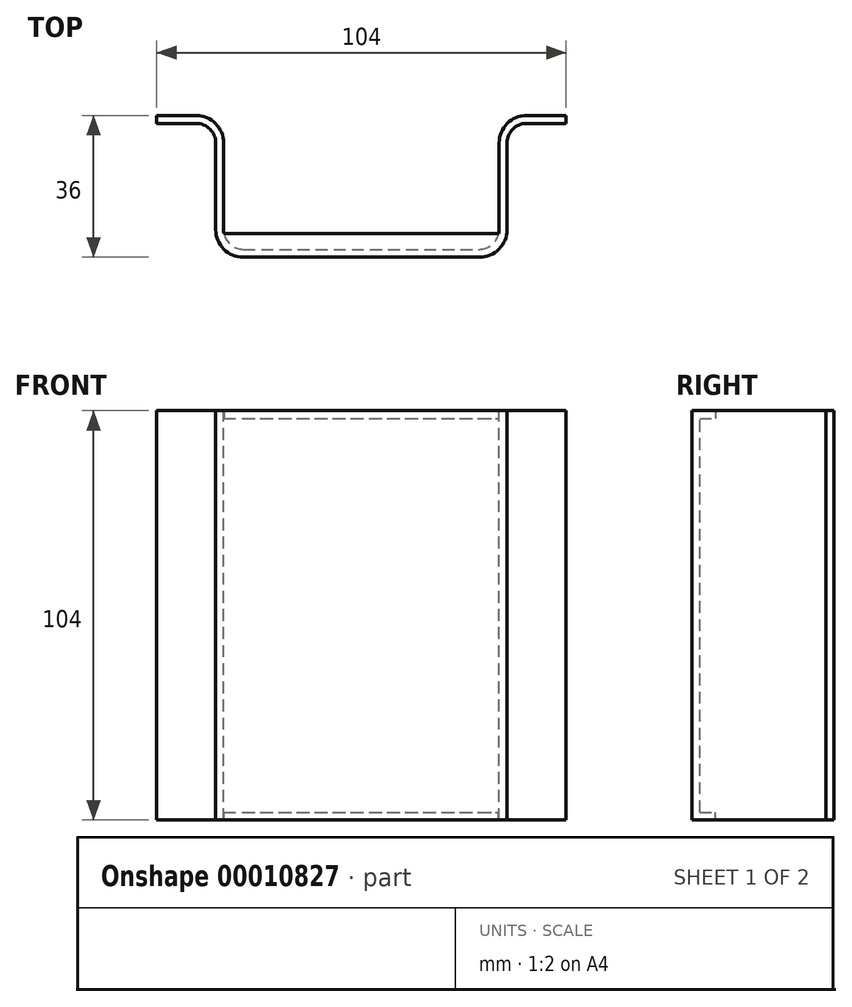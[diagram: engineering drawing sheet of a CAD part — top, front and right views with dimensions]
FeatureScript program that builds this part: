
annotation { "Feature Type Name" : "Feature", "Feature Type Description" : "" }
export const myFeature = defineFeature(function(context is Context, id is Id, definition is map)
    precondition{}
    {
        {
            var Q0;
            Q0=qCreatedBy(makeId("Top.planeOp"),FACE);
            var sketch = newSketch(context, id + "F0", { "sketchPlane" : qUnion([Q0])});
            skLineSegment(sketch, "E0", {"start": v(0, 0) * mm, "end": v(30, 0) * mm});
            skLineSegment(sketch, "E1", {"start": v(37, 7) * mm, "end": v(37, 29) * mm});
            skLineSegment(sketch, "E2", {"start": v(42, 34) * mm, "end": v(52, 34) * mm});
            skLineSegment(sketch, "E3.0", {"start": v(42, 36) * mm, "end": v(52, 36) * mm});
            skLineSegment(sketch, "E3.1", {"start": v(35, 7) * mm, "end": v(35, 29) * mm});
            skLineSegment(sketch, "E3.2", {"start": v(0, 2) * mm, "end": v(30, 2) * mm});
            skLineSegment(sketch, "E4", {"start": v(0, 2) * mm, "end": v(0, 0) * mm, "construction": true});
            skLineSegment(sketch, "E5", {"start": v(52, 36) * mm, "end": v(52, 34) * mm});
            skPoint(sketch, "E6.visualSharp", {"position": v(35, 2) * mm});
            skArc(sketch, "E6.filletArc", {"start": v(30, 2) * mm, "mid": v(33.54, 3.46) * mm, "end": v(35, 7) * mm});
            skPoint(sketch, "E7.visualSharp", {"position": v(37, 0) * mm});
            skArc(sketch, "E7.filletArc", {"start": v(30, 0) * mm, "mid": v(34.95, 2.05) * mm, "end": v(37, 7) * mm});
            skPoint(sketch, "E8.visualSharp", {"position": v(37, 34) * mm});
            skArc(sketch, "E8.filletArc", {"start": v(42, 34) * mm, "mid": v(38.46, 32.54) * mm, "end": v(37, 29) * mm});
            skPoint(sketch, "E9.visualSharp", {"position": v(35, 36) * mm});
            skArc(sketch, "E9.filletArc", {"start": v(42, 36) * mm, "mid": v(37.05, 33.95) * mm, "end": v(35, 29) * mm});
            skLineSegment(sketch, "E10.0.MirrorCS", {"start": v(0, 2) * mm, "end": v(-30, 2) * mm});
            skLineSegment(sketch, "E11.0.MirrorCS", {"start": v(0, 0) * mm, "end": v(-30, 0) * mm});
            skArc(sketch, "E12.0.MirrorCS", {"start": v(-30, 2) * mm, "mid": v(-33.54, 3.46) * mm, "end": v(-35, 7) * mm});
            skArc(sketch, "E13.0.MirrorCS", {"start": v(-30, 0) * mm, "mid": v(-34.95, 2.05) * mm, "end": v(-37, 7) * mm});
            skLineSegment(sketch, "E14.0.MirrorCS", {"start": v(-35, 7) * mm, "end": v(-35, 29) * mm});
            skLineSegment(sketch, "E15.0.MirrorCS", {"start": v(-37, 7) * mm, "end": v(-37, 29) * mm});
            skArc(sketch, "E16.0.MirrorCS", {"start": v(-42, 36) * mm, "mid": v(-37.05, 33.95) * mm, "end": v(-35, 29) * mm});
            skArc(sketch, "E17.0.MirrorCS", {"start": v(-42, 34) * mm, "mid": v(-38.46, 32.54) * mm, "end": v(-37, 29) * mm});
            skLineSegment(sketch, "E18.0.MirrorCS", {"start": v(-42, 36) * mm, "end": v(-52, 36) * mm});
            skLineSegment(sketch, "E19.0.MirrorCS", {"start": v(-42, 34) * mm, "end": v(-52, 34) * mm});
            skLineSegment(sketch, "E20.0.MirrorCS", {"start": v(-52, 36) * mm, "end": v(-52, 34) * mm});
            skLineSegment(sketch, "E21", {"start": v(-34.9, 6) * mm, "end": v(34.9, 6) * mm});
            skSolve(sketch);
        }
        {
            var Q0;
            Q0=makeQuery(id+"F0.imprint","IMPRINT",FACE,{"disambiguationData":[TD([[makeQuery(id+"F0.imprint","IMPRINT",EDGE,{"derivedFrom":sQuery(id+"F0.wireOp",EDGE,"E0")}),1.0]])]});
            extrude(context, id + "F1", {"entities" : qUnion([Q0]), "oppositeDirection" : true, "depth" : (100 / 2) * mm});
        }
        {
            var Q0;
            Q0=makeQuery(id+"F0.imprint","IMPRINT",FACE,{"disambiguationData":[TD([[makeQuery(id+"F0.imprint","IMPRINT",EDGE,{"derivedFrom":sQuery(id+"F0.wireOp",EDGE,"E0")}),1.0]])]});
            var Q1;
            {var subQ4=sQuery(id+"F0.wireOp",EDGE,"E3.2");Q1=makeQuery(id+"F0.imprint","IMPRINT",FACE,{"disambiguationData":[TD([[makeQuery(id+"F0.imprint","IMPRINT",EDGE,{"derivedFrom":subQ4}),1.0]])]});}
            extrude(context, id + "F2", {"entities" : qUnion([Q0, Q1]), "operationType" : NewBodyOperationType.ADD, "depth" : 2 * mm});
        }
        {
            var Q0;
            Q0=makeQuery(id+"F1.opExtrude","SWEPT_BODY",BODY,{"disambiguationData":[OSD([sQuery(id+"F0.wireOp",EDGE,"E0"),sQuery(id+"F0.wireOp",EDGE,"E1"),sQuery(id+"F0.wireOp",EDGE,"E2"),sQuery(id+"F0.wireOp",EDGE,"E3.0"),sQuery(id+"F0.wireOp",EDGE,"E3.1"),sQuery(id+"F0.wireOp",EDGE,"E3.2"),sQuery(id+"F0.wireOp",EDGE,"E5"),sQuery(id+"F0.wireOp",EDGE,"E6.filletArc"),sQuery(id+"F0.wireOp",EDGE,"E7.filletArc"),sQuery(id+"F0.wireOp",EDGE,"E8.filletArc"),sQuery(id+"F0.wireOp",EDGE,"E9.filletArc"),sQuery(id+"F0.wireOp",EDGE,"E10.0.MirrorCS"),sQuery(id+"F0.wireOp",EDGE,"E11.0.MirrorCS"),sQuery(id+"F0.wireOp",EDGE,"E12.0.MirrorCS"),sQuery(id+"F0.wireOp",EDGE,"E13.0.MirrorCS"),sQuery(id+"F0.wireOp",EDGE,"E14.0.MirrorCS"),sQuery(id+"F0.wireOp",EDGE,"E15.0.MirrorCS"),sQuery(id+"F0.wireOp",EDGE,"E16.0.MirrorCS"),sQuery(id+"F0.wireOp",EDGE,"E17.0.MirrorCS"),sQuery(id+"F0.wireOp",EDGE,"E18.0.MirrorCS"),sQuery(id+"F0.wireOp",EDGE,"E19.0.MirrorCS"),sQuery(id+"F0.wireOp",EDGE,"E20.0.MirrorCS")])]});
            var Q1;
            Q1=makeQuery(id+"F1.opExtrude","CAP_FACE",FACE,{"disambiguationData":[OSD([sQuery(id+"F0.wireOp",EDGE,"E0"),sQuery(id+"F0.wireOp",EDGE,"E1"),sQuery(id+"F0.wireOp",EDGE,"E2"),sQuery(id+"F0.wireOp",EDGE,"E3.0"),sQuery(id+"F0.wireOp",EDGE,"E3.1"),sQuery(id+"F0.wireOp",EDGE,"E3.2"),sQuery(id+"F0.wireOp",EDGE,"E5"),sQuery(id+"F0.wireOp",EDGE,"E6.filletArc"),sQuery(id+"F0.wireOp",EDGE,"E7.filletArc"),sQuery(id+"F0.wireOp",EDGE,"E8.filletArc"),sQuery(id+"F0.wireOp",EDGE,"E9.filletArc"),sQuery(id+"F0.wireOp",EDGE,"E10.0.MirrorCS"),sQuery(id+"F0.wireOp",EDGE,"E11.0.MirrorCS"),sQuery(id+"F0.wireOp",EDGE,"E12.0.MirrorCS"),sQuery(id+"F0.wireOp",EDGE,"E13.0.MirrorCS"),sQuery(id+"F0.wireOp",EDGE,"E14.0.MirrorCS"),sQuery(id+"F0.wireOp",EDGE,"E15.0.MirrorCS"),sQuery(id+"F0.wireOp",EDGE,"E16.0.MirrorCS"),sQuery(id+"F0.wireOp",EDGE,"E17.0.MirrorCS"),sQuery(id+"F0.wireOp",EDGE,"E18.0.MirrorCS"),sQuery(id+"F0.wireOp",EDGE,"E19.0.MirrorCS"),sQuery(id+"F0.wireOp",EDGE,"E20.0.MirrorCS")])],"isStart":false});
            mirror(context, id + "F3", {"operationType" : NewBodyOperationType.ADD, "entities" : qUnion([Q0]), "mirrorPlane" : qUnion([Q1])});
        }
    });
